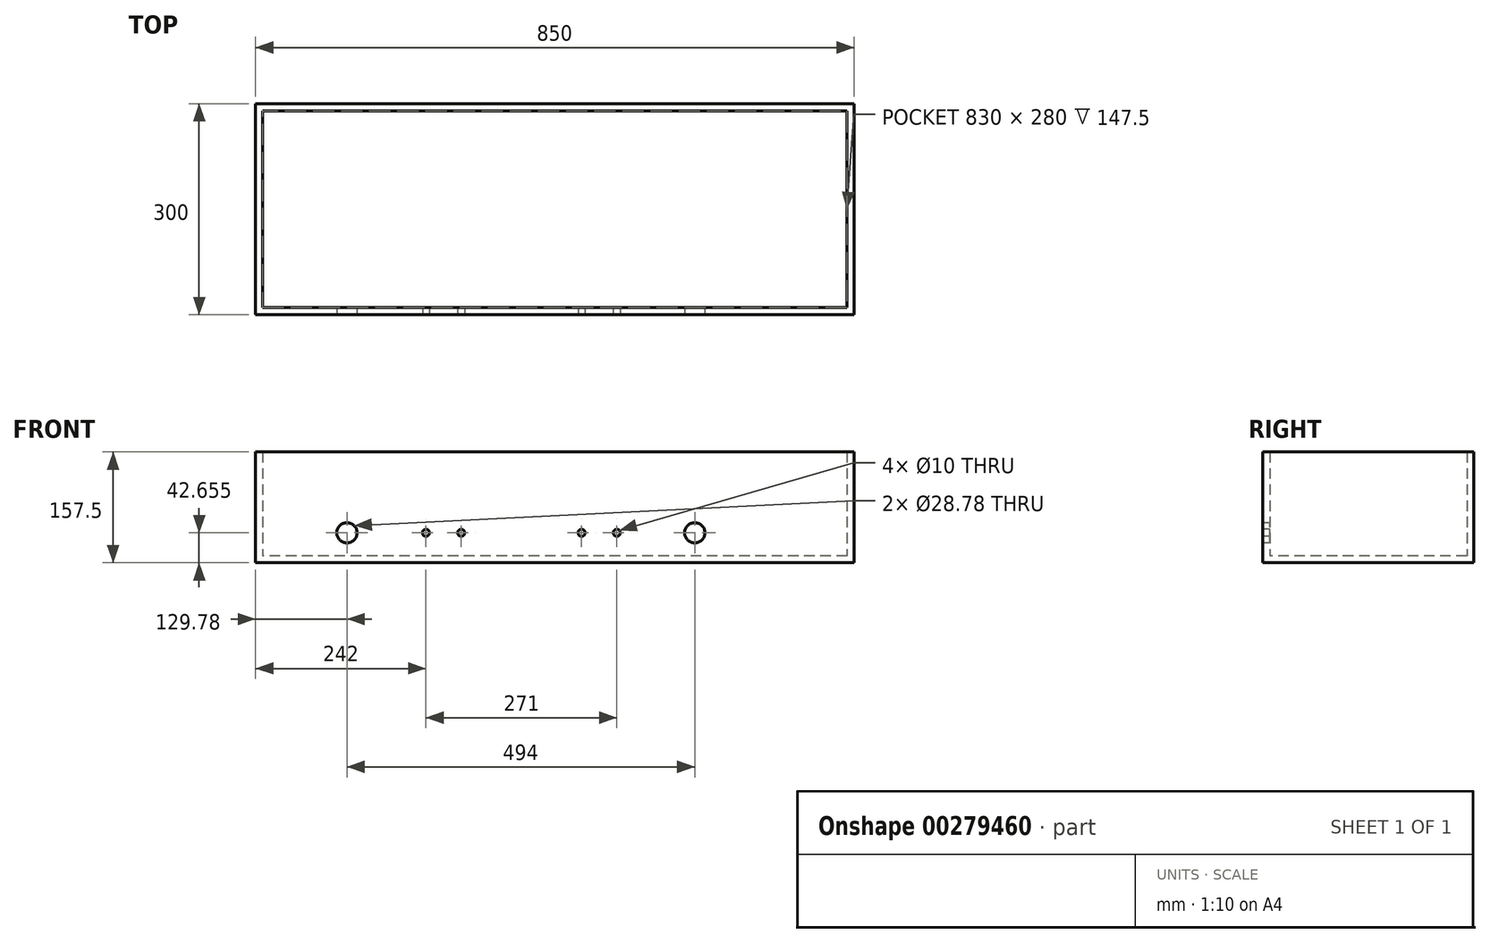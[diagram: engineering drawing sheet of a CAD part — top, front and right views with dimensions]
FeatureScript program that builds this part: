
annotation { "Feature Type Name" : "Feature", "Feature Type Description" : "" }
export const myFeature = defineFeature(function(context is Context, id is Id, definition is map)
    precondition{}
    {
        {
            var Q0;
            Q0=qCreatedBy(makeId("Top.planeOp"),FACE);
            var sketch = newSketch(context, id + "F0", { "sketchPlane" : qUnion([Q0])});
            skLineSegment(sketch, "E0.bottom", {"start": v(425, 150) * mm, "end": v(-425, 150) * mm});
            skLineSegment(sketch, "E0.top", {"start": v(425, -150) * mm, "end": v(-425, -150) * mm});
            skLineSegment(sketch, "E0.left", {"start": v(425, 150) * mm, "end": v(425, -150) * mm});
            skLineSegment(sketch, "E0.right", {"start": v(-425, 150) * mm, "end": v(-425, -150) * mm});
            skPoint(sketch, "E0.middle", {"position": v(0, 0) * mm});
            skSolve(sketch);
        }
        {
            var Q0;
            Q0=makeQuery(id+"F0.imprint","IMPRINT",FACE,{"disambiguationData":[TD([[makeQuery(id+"F0.imprint","IMPRINT",EDGE,{"derivedFrom":sQuery(id+"F0.wireOp",EDGE,"E0.bottom")}),1.0]])]});
            extrude(context, id + "F1", {"entities" : qUnion([Q0]), "depth" : 7.5 * mm});
        }
        {
            var Q0;
            Q0=makeQuery(id+"F1.opExtrude","CAP_FACE",FACE,{"disambiguationData":[OSD([sQuery(id+"F0.wireOp",EDGE,"E0.bottom"),sQuery(id+"F0.wireOp",EDGE,"E0.top"),sQuery(id+"F0.wireOp",EDGE,"E0.left"),sQuery(id+"F0.wireOp",EDGE,"E0.right")])],"isStart":false});
            var sketch = newSketch(context, id + "F2", { "sketchPlane" : qUnion([Q0])});
            skLineSegment(sketch, "E1.bottom", {"start": v(417.5, 142.5) * mm, "end": v(-417.5, 142.5) * mm});
            skLineSegment(sketch, "E1.top", {"start": v(417.5, -142.5) * mm, "end": v(-417.5, -142.5) * mm});
            skLineSegment(sketch, "E1.left", {"start": v(417.5, 142.5) * mm, "end": v(417.5, -142.5) * mm});
            skLineSegment(sketch, "E1.right", {"start": v(-417.5, 142.5) * mm, "end": v(-417.5, -142.5) * mm});
            skPoint(sketch, "E1.middle", {"position": v(0, 0) * mm});
            skLineSegment(sketch, "E2.bottom", {"start": v(425, 150) * mm, "end": v(-425, 150) * mm});
            skLineSegment(sketch, "E2.top", {"start": v(425, -150) * mm, "end": v(-425, -150) * mm});
            skLineSegment(sketch, "E2.left", {"start": v(425, 150) * mm, "end": v(425, -150) * mm});
            skLineSegment(sketch, "E2.right", {"start": v(-425, 150) * mm, "end": v(-425, -150) * mm});
            skSolve(sketch);
        }
        {
            var Q0;
            Q0=qSketchRegion(id+"F2",true);
            extrude(context, id + "F3", {"entities" : qUnion([Q0]), "operationType" : NewBodyOperationType.ADD, "depth" : 150 * mm});
        }
        {
            var Q0;
            Q0=makeQuery(id+"F1.opExtrude","CAP_FACE",FACE,{"disambiguationData":[OSD([sQuery(id+"F0.wireOp",EDGE,"E0.bottom"),sQuery(id+"F0.wireOp",EDGE,"E0.top"),sQuery(id+"F0.wireOp",EDGE,"E0.left"),sQuery(id+"F0.wireOp",EDGE,"E0.right")])],"isStart":false});
            extrude(context, id + "F4", {"entities" : qUnion([Q0]), "depth" : 2.5 * mm});
        }
        {
            var Q0;
            Q0=makeQuery(id+"F4.opExtrude","CAP_FACE",FACE,{"disambiguationData":[OSD([sQuery(id+"F0.wireOp",EDGE,"E0.bottom"),sQuery(id+"F0.wireOp",EDGE,"E0.top"),sQuery(id+"F0.wireOp",EDGE,"E0.left"),sQuery(id+"F0.wireOp",EDGE,"E0.right")])],"isStart":false});
            var sketch = newSketch(context, id + "F5", { "sketchPlane" : qUnion([Q0])});
            skLineSegment(sketch, "E3.bottom", {"start": v(415, 140) * mm, "end": v(-415, 140) * mm});
            skLineSegment(sketch, "E3.top", {"start": v(415, -140) * mm, "end": v(-415, -140) * mm});
            skLineSegment(sketch, "E3.left", {"start": v(415, 140) * mm, "end": v(415, -140) * mm});
            skLineSegment(sketch, "E3.right", {"start": v(-415, 140) * mm, "end": v(-415, -140) * mm});
            skPoint(sketch, "E3.middle", {"position": v(0, 0) * mm});
            skLineSegment(sketch, "E4.bottom", {"start": v(417.5, 142.5) * mm, "end": v(-417.5, 142.5) * mm});
            skLineSegment(sketch, "E4.top", {"start": v(417.5, -142.5) * mm, "end": v(-417.5, -142.5) * mm});
            skLineSegment(sketch, "E4.left", {"start": v(417.5, 142.5) * mm, "end": v(417.5, -142.5) * mm});
            skLineSegment(sketch, "E4.right", {"start": v(-417.5, 142.5) * mm, "end": v(-417.5, -142.5) * mm});
            skSolve(sketch);
        }
        {
            var Q0;
            Q0=qSketchRegion(id+"F5",true);
            extrude(context, id + "F6", {"entities" : qUnion([Q0]), "operationType" : NewBodyOperationType.ADD, "depth" : 147.5 * mm});
        }
        {
            var Q0;
            Q0=makeQuery(id+"F3.boolean.opBoolean","MERGE",FACE,{"derivedFrom":[makeQuery(id+"F1.opExtrude","SWEPT_FACE",FACE,{"disambiguationData":[OSD([sQuery(id+"F0.wireOp",EDGE,"E0.top")])]}),makeQuery(id+"F3.opExtrude","SWEPT_FACE",FACE,{"disambiguationData":[OSD([sQuery(id+"F2.wireOp",EDGE,"E2.top")])]})]});
            var sketch = newSketch(context, id + "F7", { "sketchPlane" : qUnion([Q0])});
            skLineSegment(sketch, "E5.bottom", {"start": v(280, 144.85) * mm, "end": v(-395, 144.84) * mm, "construction": true});
            skLineSegment(sketch, "E5.top", {"start": v(280, 12.66) * mm, "end": v(-395, 12.66) * mm, "construction": true});
            skLineSegment(sketch, "E5.left", {"start": v(280, 144.85) * mm, "end": v(280, 12.66) * mm, "construction": true});
            skLineSegment(sketch, "E5.right", {"start": v(-395, 144.84) * mm, "end": v(-395, 12.66) * mm, "construction": true});
            skPoint(sketch, "E5.middle", {"position": v(0, 78.75) * mm});
            skPoint(sketch, "E5.middle.positionSnap0", {"position": v(-425, 78.75) * mm});
            skPoint(sketch, "E5.centerSnap0", {"position": v(-425, 78.75) * mm});
            skCircle(sketch, "E6", {"center": v(-133, 42.65) * mm, "radius": 5 * mm});
            skCircle(sketch, "E7", {"center": v(38, 42.66) * mm, "radius": 5 * mm});
            skLineSegment(sketch, "E8", {"start": v(-133, 42.65) * mm, "end": v(-133, 12.65) * mm, "construction": true});
            skLineSegment(sketch, "E9", {"start": v(-133, 42.65) * mm, "end": v(-395, 42.65) * mm, "construction": true});
            skLineSegment(sketch, "E10", {"start": v(38, 42.66) * mm, "end": v(38, 12.66) * mm, "construction": true});
            skLineSegment(sketch, "E11", {"start": v(38, 42.66) * mm, "end": v(280, 42.66) * mm, "construction": true});
            skCircle(sketch, "E12.1.0.0", {"center": v(88, 42.66) * mm, "radius": 5 * mm});
            skLineSegment(sketch, "E12.direction1", {"start": v(38, 42.66) * mm, "end": v(88, 42.66) * mm, "construction": true});
            skCircle(sketch, "E13.1.0.0", {"center": v(-183, 42.65) * mm, "radius": 5 * mm});
            skLineSegment(sketch, "E13.direction1", {"start": v(-133, 42.65) * mm, "end": v(-183, 42.65) * mm, "construction": true});
            skCircle(sketch, "E14", {"center": v(198.78, 42.66) * mm, "radius": 14.4 * mm});
            skCircle(sketch, "E15.1.0.0", {"center": v(-295.22, 42.65) * mm, "radius": 14.4 * mm});
            skLineSegment(sketch, "E15.direction1", {"start": v(198.78, 42.66) * mm, "end": v(-295.22, 42.66) * mm, "construction": true});
            skSolve(sketch);
        }
        {
            var Q0;
            Q0=qSketchRegion(id+"F7",true);
            extrude(context, id + "F8", {"entities" : qUnion([Q0]), "operationType" : NewBodyOperationType.REMOVE, "oppositeDirection" : true, "depth" : 25 * mm});
        }
    });
